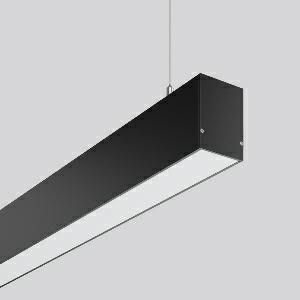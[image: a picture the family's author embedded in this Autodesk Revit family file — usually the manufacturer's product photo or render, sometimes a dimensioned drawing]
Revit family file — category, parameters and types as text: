
# Revit family: less_is_more_50_312319_003_1_f851
name_source: partatom
category: Lighting Fixtures
units: mm (PartAtom-declared; Revit-internal decimal feet)

## family parameters
Cut with Voids When Loaded = No
Host = Face
Light Source = No
Part Type = Normal
Room Calculation Point = No
Round Connector Dimension = Use Diameter
Shared = No

## types (1)
- LESS IS MORE 50 (1 x LED Modul 840, 6450 lm, 4000)
    Apparent Load = 52 VA
    CIE Flux Codes = 49 80 96 63 100
    Color Rendering = 80
    Color Temperature = 4000
    Default Elevation = 1800 mm
    Description = Series: LESS IS MORE 50
Linear pendant luminaire for aesthetically sophisticated lighting. Housing: extruded aluminium profile, powder-coated. End cap aluminium powder-coated. Canopy made of aluminium, powder-coated. Diffuser made of non-yellowing plastic (PMMA), opal. Direct 65%, indirect 35% light emission. Suitable for pendant. 2-point steel cable suspension freely positionable and infinitely height-adjustable. Special lengths available on request. LED unit with integrated converter interchangeable and removable. Suitable for through-wiring. With sensors or as a safety luminaire on request. 
Colour: deep black, matt (RAL 9005)
Length: 1407 mm
Width: 57 mm
Height: 75 mm
Suspension length: 2000 mm
Lamp: LED
Socket: without socket
Colour temperature: 4000K
Colour rendering index (CRI): 80
Light source: LED
Socket lamp2: Without base
Colour temperature: 4000K
System power: 52 W
Rated luminous flux: 6450 lm
Luminous efficiency: 124 lm/W
Control gear: Regulated power supply
Control gear: Regulated power supply
Protection class: I
Type of protection: IP 20
    Height = 75 mm
    Lamp = 1 x LED Modul 840
    Lamp Light Flux = 6450 lm
    Lamp count = 1
    Length = 1407 mm
    Lifetime = 50000 h
    Luminous efficacy = 124 lm/W
    Manufacturer = RZB
    ModVariant = No
    Model = 312319.003.1
    Mounting Place = Ceiling
    Mounting Type = Pendant
    Number of Poles = 1
    OnlyDefault = Yes
    Power Factor = 1
    Product Name = LESS IS MORE 50
    Product group = Pendant LED linear luminaires
    ProductGroupID = 907
    Protection Class = Protection class I
    Protection Degree = IP 20
    RLX_Detail_Level = 1
    RLX_Emergency_Light_Flux = 0 lm
    RLX_Emergency_Type = 0
    RLX_Emergency_Type_DB = No
    RlxData = <blob elided: 39881 chars, md5=6ac355ca>
    Socket = socket
    Standby Power = 0 W
    System Light Flux = 6450 lm
    System Power = 52 W
    Type Comments = Product without accessories
    Type Image = 312318.003.jpg
    URL = http://relux.com
    VarID = ---
    Voltage = 230 V
    Voltage Range = 220-240 V
    Weight = 0.00 kg
    Width = 57 mm

## geometry (parser evidence)
native form markers: Blend x4, Sweep x12
no freeform markers — native parametric forms only
